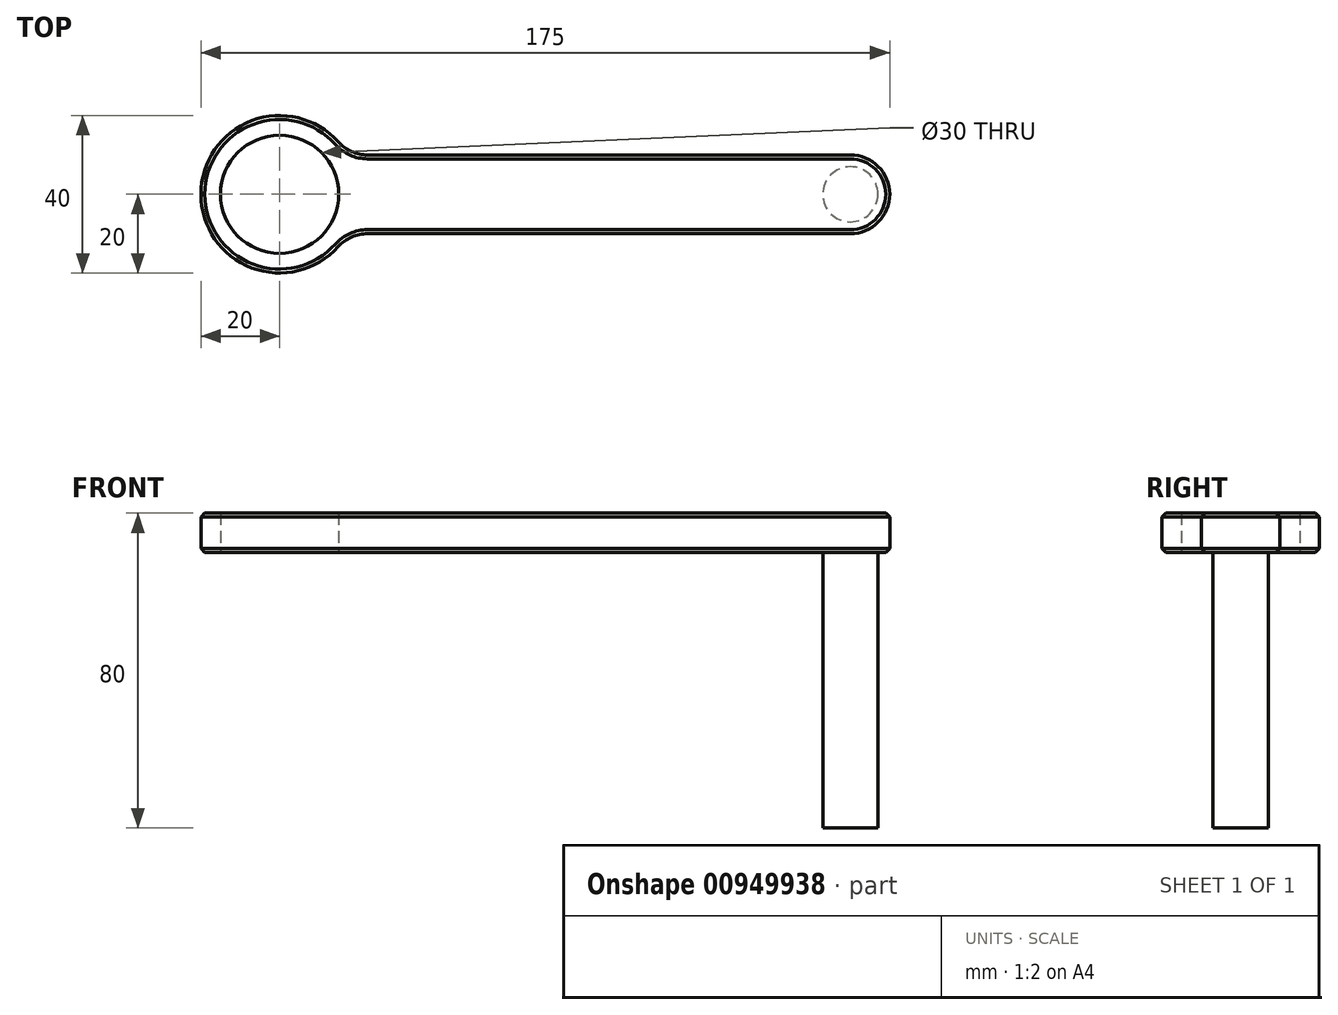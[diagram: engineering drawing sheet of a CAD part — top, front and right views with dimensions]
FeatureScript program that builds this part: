
annotation { "Feature Type Name" : "Feature", "Feature Type Description" : "" }
export const myFeature = defineFeature(function(context is Context, id is Id, definition is map)
    precondition{}
    {
        {
            var Q0;
            Q0=qCreatedBy(makeId("Top.planeOp"),FACE);
            var sketch = newSketch(context, id + "F0", { "sketchPlane" : qUnion([Q0])});
            skLineSegment(sketch, "E0.bottom", {"start": v(0, 0) * mm, "end": v(-165, 0) * mm});
            skLineSegment(sketch, "E0.top", {"start": v(0, -20) * mm, "end": v(-165, -20) * mm});
            skLineSegment(sketch, "E0.left", {"start": v(0, 0) * mm, "end": v(0, -20) * mm});
            skLineSegment(sketch, "E0.right", {"start": v(-165, 0) * mm, "end": v(-165, -20) * mm});
            skCircle(sketch, "E1", {"center": v(-155, -10) * mm, "radius": 15 * mm});
            skCircle(sketch, "E2", {"center": v(-10, -10) * mm, "radius": 7 * mm});
            skCircle(sketch, "E3", {"center": v(-155, -10) * mm, "radius": 20 * mm});
            skSolve(sketch);
        }
        {
            var Q0;
            {var subQ0=sQuery(id+"F0.wireOp",EDGE,"E0.left");Q0=makeQuery(id+"F0.imprint","IMPRINT",FACE,{"disambiguationData":[TD([[makeQuery(id+"F0.imprint","IMPRINT",EDGE,{"derivedFrom":subQ0}),-1.0]])]});}
            var Q1;
            {var subQ0=sQuery(id+"F0.wireOp",EDGE,"E3");var subQ1=sQuery(id+"F0.wireOp",EDGE,"E0.bottom");var subQ2=makeQuery(id+"F0.imprint","INTERSECT",VERTEX,{"derivedFrom":[subQ1,subQ0]});Q1=makeQuery(id+"F0.imprint","IMPRINT",FACE,{"disambiguationData":[TD([[makeQuery(id+"F0.imprint","IMPRINT",EDGE,{"disambiguationData":[TD([[subQ2,-1.0]])],"derivedFrom":subQ1}),-1.0]])]});}
            var Q2;
            {var subQ0=sQuery(id+"F0.wireOp",EDGE,"E3");var subQ1=sQuery(id+"F0.wireOp",EDGE,"E0.bottom");var subQ2=makeQuery(id+"F0.imprint","INTERSECT",VERTEX,{"derivedFrom":[subQ1,subQ0]});Q2=makeQuery(id+"F0.imprint","IMPRINT",FACE,{"disambiguationData":[TD([[makeQuery(id+"F0.imprint","IMPRINT",EDGE,{"disambiguationData":[TD([[subQ2,-1.0]])],"derivedFrom":subQ1}),1.0]])]});}
            extrude(context, id + "F1", {"entities" : qUnion([Q0, Q1, Q2]), "depth" : 10 * mm, "offsetDistance" : 25 * mm});
        }
        {
            var Q0;
            Q0=makeQuery(id+"F0.imprint","IMPRINT",FACE,{"disambiguationData":[TD([[makeQuery(id+"F0.imprint","IMPRINT",EDGE,{"derivedFrom":sQuery(id+"F0.wireOp",EDGE,"E1")}),1.0]])]});
            var Q1;
            Q1=makeQuery(id+"F0.imprint","IMPRINT",FACE,{"disambiguationData":[TD([[makeQuery(id+"F0.imprint","IMPRINT",EDGE,{"derivedFrom":sQuery(id+"F0.wireOp",EDGE,"E2")}),1.0]])]});
            extrude(context, id + "F2", {"entities" : qUnion([Q0, Q1]), "operationType" : NewBodyOperationType.REMOVE, "endBound" : BoundingType.THROUGH_ALL, "depth" : 25 * mm, "offsetDistance" : 25 * mm});
        }
        {
            var Q0;
            Q0=makeQuery(id+"F1.opExtrude","SWEPT_EDGE",EDGE,{"disambiguationData":[OSD([sQuery(id+"F0.wireOp",EDGE,"E0.top"),sQuery(id+"F0.wireOp",EDGE,"E0.right")])]});
            var Q1;
            Q1=makeQuery(id+"F1.opExtrude","SWEPT_EDGE",EDGE,{"disambiguationData":[OSD([sQuery(id+"F0.wireOp",EDGE,"E0.bottom"),sQuery(id+"F0.wireOp",EDGE,"E0.right")])]});
            var Q2;
            Q2=makeQuery(id+"F1.opExtrude","SWEPT_EDGE",EDGE,{"disambiguationData":[OSD([sQuery(id+"F0.wireOp",EDGE,"E0.top"),sQuery(id+"F0.wireOp",EDGE,"E0.left")])]});
            var Q3;
            Q3=makeQuery(id+"F1.opExtrude","SWEPT_EDGE",EDGE,{"disambiguationData":[OSD([sQuery(id+"F0.wireOp",EDGE,"E0.bottom"),sQuery(id+"F0.wireOp",EDGE,"E0.left")])]});
            fillet(context, id + "F3", {"entities" : qUnion([Q0, Q1, Q2, Q3]), "radius" : 10 * mm, "tangentPropagation" : true, "allowEdgeOverflow" : false});
        }
        {
            var Q0;
            Q0=makeQuery(id+"F1.opExtrude","CAP_EDGE",EDGE,{"disambiguationData":[OSD([sQuery(id+"F0.wireOp",EDGE,"E0.top")])],"isStart":true});
            var Q1;
            {var subQ0=sQuery(id+"F0.wireOp",EDGE,"E0.left");var subQ1=sQuery(id+"F0.wireOp",EDGE,"E0.bottom");Q1=makeQuery(id+"F3.opFillet","BLEND_EDGE",EDGE,{"blendedFrom":[makeQuery(id+"F1.opExtrude","SWEPT_EDGE",EDGE,{"disambiguationData":[OSD([subQ1,subQ0])]}),makeQuery(id+"F1.opExtrude","CAP_FACE",FACE,{"disambiguationData":[OSD([subQ1,sQuery(id+"F0.wireOp",EDGE,"E0.top"),subQ0,sQuery(id+"F0.wireOp",EDGE,"E0.right")])],"isStart":false})],"blendedInto":[makeQuery(id+"F1.opExtrude","CAP_FACE",FACE,{"disambiguationData":[OSD([subQ1,sQuery(id+"F0.wireOp",EDGE,"E0.top"),subQ0,sQuery(id+"F0.wireOp",EDGE,"E0.right")])],"isStart":false})]});}
            chamfer(context, id + "F4", {"entities" : qUnion([Q0, Q1]), "width" : 1 * mm, "tangentPropagation" : true});
        }
        {
            var Q0;
            Q0=makeQuery(id+"F1.opExtrude","CAP_FACE",FACE,{"disambiguationData":[OSD([sQuery(id+"F0.wireOp",EDGE,"E0.bottom"),sQuery(id+"F0.wireOp",EDGE,"E0.top"),sQuery(id+"F0.wireOp",EDGE,"E0.left"),sQuery(id+"F0.wireOp",EDGE,"E1"),sQuery(id+"F0.wireOp",EDGE,"E2"),sQuery(id+"F0.wireOp",EDGE,"E3")])],"isStart":false});
            var sketch = newSketch(context, id + "F5", { "sketchPlane" : qUnion([Q0])});
            skSolve(sketch);
        }
        {
            var Q0;
            Q0=makeQuery(id+"F5.imprint","IMPRINT",FACE,{"disambiguationData":[TD([[makeQuery(id+"F5.imprint","IMPRINT",EDGE,{"derivedFrom":makeQuery(id+"F1.opExtrude","CAP_EDGE",EDGE,{"disambiguationData":[OSD([sQuery(id+"F0.wireOp",EDGE,"E2")])],"isStart":false})}),1.0]])]});
            extrude(context, id + "F6", {"entities" : qUnion([Q0]), "operationType" : NewBodyOperationType.ADD, "oppositeDirection" : true, "depth" : 80 * mm, "offsetDistance" : 25 * mm});
        }
    });
